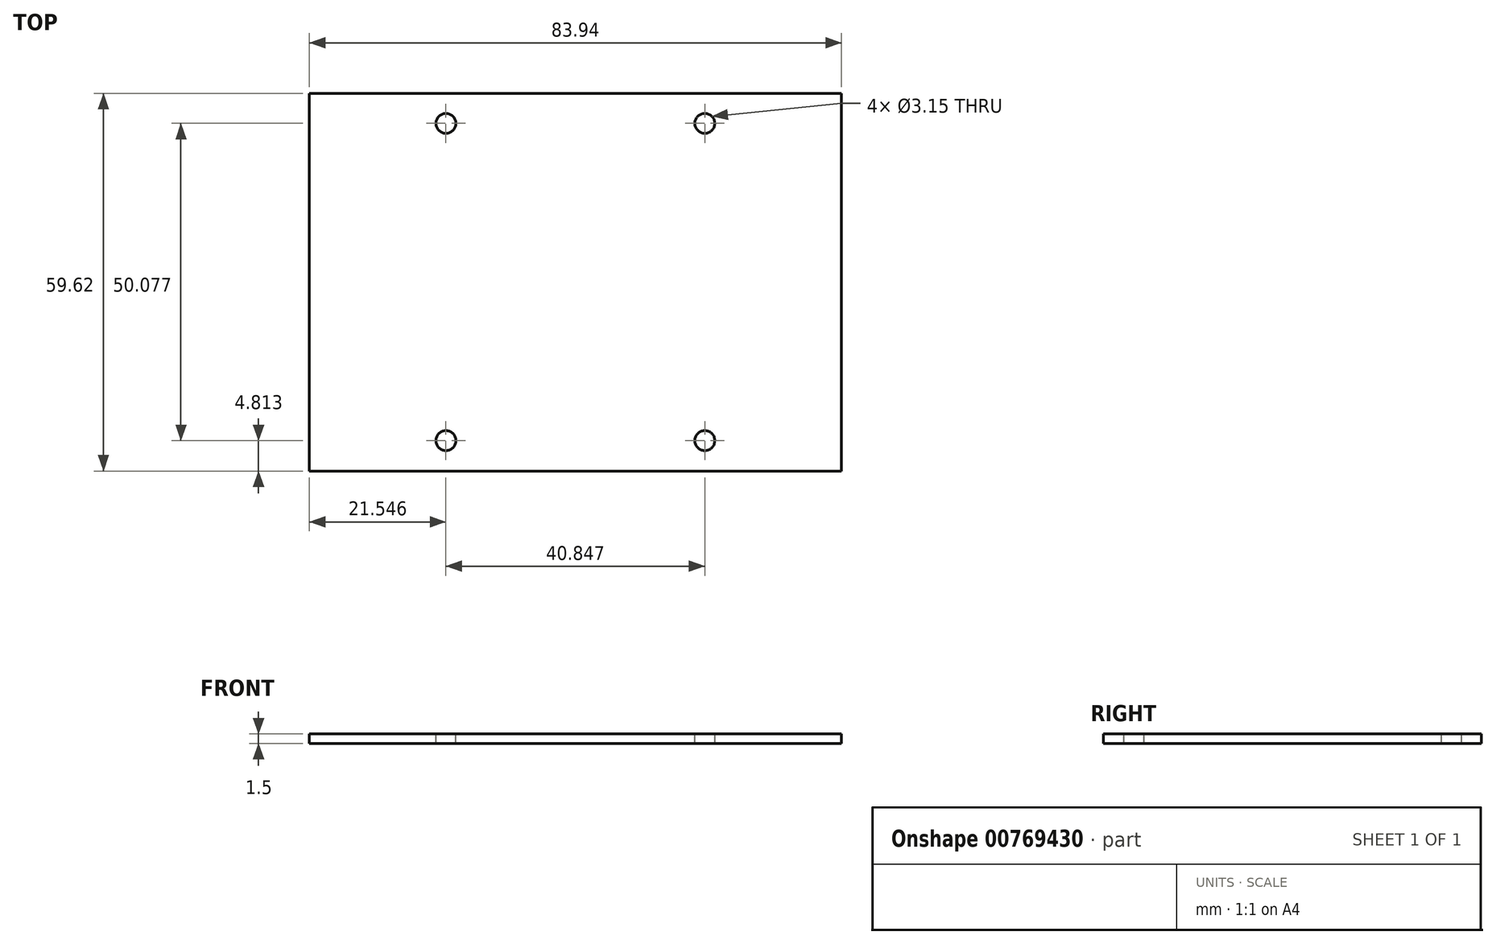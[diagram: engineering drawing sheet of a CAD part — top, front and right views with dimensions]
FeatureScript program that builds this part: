
annotation { "Feature Type Name" : "Feature", "Feature Type Description" : "" }
export const myFeature = defineFeature(function(context is Context, id is Id, definition is map)
    precondition{}
    {
        {
            var Q0;
            Q0=qCreatedBy(makeId("Top.planeOp"),FACE);
            var sketch = newSketch(context, id + "F0", { "sketchPlane" : qUnion([Q0])});
            skLineSegment(sketch, "E0.bottom", {"start": v(41.97, 29.8) * mm, "end": v(-41.97, 29.8) * mm});
            skLineSegment(sketch, "E0.top", {"start": v(41.97, -29.8) * mm, "end": v(-41.97, -29.8) * mm});
            skLineSegment(sketch, "E0.left", {"start": v(41.97, 29.8) * mm, "end": v(41.97, -29.8) * mm});
            skLineSegment(sketch, "E0.right", {"start": v(-41.97, 29.8) * mm, "end": v(-41.97, -29.8) * mm});
            skPoint(sketch, "E0.middle", {"position": v(0, 0) * mm});
            skPoint(sketch, "E1", {"position": v(-20.42, -29.8) * mm});
            skPoint(sketch, "E2", {"position": v(-41.97, -25) * mm});
            skPoint(sketch, "E3", {"position": v(-20.42, -25) * mm});
            skPoint(sketch, "E4", {"position": v(41.97, -25) * mm});
            skPoint(sketch, "E5", {"position": v(20.42, -29.8) * mm});
            skPoint(sketch, "E6", {"position": v(20.42, -25) * mm});
            skPoint(sketch, "E7", {"position": v(20.42, 29.8) * mm});
            skPoint(sketch, "E8", {"position": v(41.97, 25) * mm});
            skPoint(sketch, "E9", {"position": v(20.42, 25) * mm});
            skPoint(sketch, "E10", {"position": v(-20.42, 25) * mm});
            skSolve(sketch);
        }
        {
            var Q0;
            Q0 = qSketchRegion(id + "F0", true);
            extrude(context, id + "F1", {"entities" : qUnion([Q0]), "depth" : 1.5 * mm, "offsetDistance" : 25.4 * mm});
        }
        {
            var Q0;
            Q0=makeQuery(id+"F1.opExtrude","CAP_FACE",FACE,{"disambiguationData":[OSD([sQuery(id+"F0.wireOp",EDGE,"E0.bottom"),sQuery(id+"F0.wireOp",EDGE,"E0.top"),sQuery(id+"F0.wireOp",EDGE,"E0.left"),sQuery(id+"F0.wireOp",EDGE,"E0.right")])],"isStart":false});
            var sketch = newSketch(context, id + "F2", { "sketchPlane" : qUnion([Q0])});
            skPoint(sketch, "E11", {"position": v(-20.42, -29.8) * mm});
            skPoint(sketch, "E12", {"position": v(-41.97, -25) * mm});
            skPoint(sketch, "E13", {"position": v(-20.42, -25) * mm});
            skPoint(sketch, "E14", {"position": v(-20.42, 29.89) * mm});
            skPoint(sketch, "E15", {"position": v(-41.97, 25.08) * mm});
            skPoint(sketch, "E16", {"position": v(-20.42, 25.08) * mm});
            skPoint(sketch, "E17", {"position": v(20.42, -29.8) * mm});
            skPoint(sketch, "E18", {"position": v(20.42, -25) * mm});
            skPoint(sketch, "E19", {"position": v(20.42, 25.08) * mm});
            skSolve(sketch);
        }
        {
            var Q0;
            Q0=sQuery(id+"F2.wireOp",VERTEX,"E13");
            var Q1;
            Q1=makeQuery(id+"F1.opExtrude","SWEPT_BODY",BODY,{"disambiguationData":[OSD([sQuery(id+"F0.wireOp",EDGE,"E0.bottom"),sQuery(id+"F0.wireOp",EDGE,"E0.top"),sQuery(id+"F0.wireOp",EDGE,"E0.left"),sQuery(id+"F0.wireOp",EDGE,"E0.right")])]});
            hole(context, id + "F3", {"style" : HoleStyle.SIMPLE, "endStyle" : HoleEndStyle.THROUGH, "standardTappedOrClearance" : lookupTablePath({ "standard" : "ISO", "fit" : "Close", "size" : "M3", "type" : "Clearance" }), "standardBlindInLast" : lookupTablePath({ "fit" : "Close", "standard" : "ISO", "size" : "M3", "type" : "Clearance" }), "holeDiameter" : 3.15 * mm, "majorDiameter" : 6.35 * mm, "isTappedThrough" : true, "tappedDepth" : 12.7 * mm, "tapClearance" : 3, "locations" : qUnion([Q0]), "scope" : qUnion([Q1])});
        }
        {
            var Q0;
            Q0=sQuery(id+"F2.wireOp",VERTEX,"E18");
            var Q1;
            Q1=makeQuery(id+"F1.opExtrude","SWEPT_BODY",BODY,{"disambiguationData":[OSD([sQuery(id+"F0.wireOp",EDGE,"E0.bottom"),sQuery(id+"F0.wireOp",EDGE,"E0.top"),sQuery(id+"F0.wireOp",EDGE,"E0.left"),sQuery(id+"F0.wireOp",EDGE,"E0.right")])]});
            hole(context, id + "F4", {"style" : HoleStyle.SIMPLE, "endStyle" : HoleEndStyle.THROUGH, "standardTappedOrClearance" : lookupTablePath({ "standard" : "ISO", "fit" : "Close", "size" : "M3", "type" : "Clearance" }), "standardBlindInLast" : lookupTablePath({ "fit" : "Close", "standard" : "ISO", "size" : "M3", "type" : "Clearance" }), "holeDiameter" : 3.15 * mm, "majorDiameter" : 6.35 * mm, "isTappedThrough" : true, "tappedDepth" : 12.7 * mm, "tapClearance" : 3, "locations" : qUnion([Q0]), "scope" : qUnion([Q1])});
        }
        {
            var Q0;
            Q0=sQuery(id+"F2.wireOp",VERTEX,"E16");
            var Q1;
            Q1=makeQuery(id+"F1.opExtrude","SWEPT_BODY",BODY,{"disambiguationData":[OSD([sQuery(id+"F0.wireOp",EDGE,"E0.bottom"),sQuery(id+"F0.wireOp",EDGE,"E0.top"),sQuery(id+"F0.wireOp",EDGE,"E0.left"),sQuery(id+"F0.wireOp",EDGE,"E0.right")])]});
            hole(context, id + "F5", {"style" : HoleStyle.SIMPLE, "endStyle" : HoleEndStyle.THROUGH, "standardTappedOrClearance" : lookupTablePath({ "standard" : "ISO", "fit" : "Close", "size" : "M3", "type" : "Clearance" }), "standardBlindInLast" : lookupTablePath({ "fit" : "Close", "standard" : "ISO", "size" : "M3", "type" : "Clearance" }), "holeDiameter" : 3.15 * mm, "majorDiameter" : 6.35 * mm, "isTappedThrough" : true, "tappedDepth" : 12.7 * mm, "tapClearance" : 3, "locations" : qUnion([Q0]), "scope" : qUnion([Q1])});
        }
        {
            var Q0;
            Q0=sQuery(id+"F2.wireOp",VERTEX,"E19");
            var Q1;
            Q1=makeQuery(id+"F1.opExtrude","SWEPT_BODY",BODY,{"disambiguationData":[OSD([sQuery(id+"F0.wireOp",EDGE,"E0.bottom"),sQuery(id+"F0.wireOp",EDGE,"E0.top"),sQuery(id+"F0.wireOp",EDGE,"E0.left"),sQuery(id+"F0.wireOp",EDGE,"E0.right")])]});
            hole(context, id + "F6", {"style" : HoleStyle.SIMPLE, "endStyle" : HoleEndStyle.THROUGH, "standardTappedOrClearance" : lookupTablePath({ "standard" : "ISO", "fit" : "Close", "size" : "M3", "type" : "Clearance" }), "standardBlindInLast" : lookupTablePath({ "fit" : "Close", "standard" : "ISO", "size" : "M3", "type" : "Clearance" }), "holeDiameter" : 3.15 * mm, "majorDiameter" : 6.35 * mm, "isTappedThrough" : true, "tappedDepth" : 12.7 * mm, "tapClearance" : 3, "locations" : qUnion([Q0]), "scope" : qUnion([Q1])});
        }
    });
